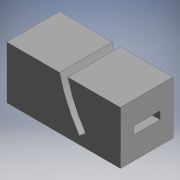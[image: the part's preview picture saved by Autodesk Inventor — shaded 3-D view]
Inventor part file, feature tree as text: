
AUTODESK INVENTOR PART (.ipt)
format: ipt  version: 2018 (Build 220112000, 112)  size: 113,664 bytes
history: native  units: in
note: dims shown in document units (in); Inventor stores cm internally (conversion verified against a paired STEP export)
features: extrude x2, sketch x2
ambient origin geometry x8: Origin, YZ Plane, XZ Plane, XY Plane, X Axis, Y Axis, Z Axis, Center Point
bodies: Solid1 (feature_tree)
feature tree (4):
  extrude  "Extrusion1"  Depth=0.3937in
  extrude  "Extrusion2"  Depth=0.3937in TaperAngle=0.0deg
  sketch  "Sketch1"  dims[d0=0.3937in d2=0.3937in]
  sketch  "Sketch2"  dims[d4=0.3937in d5=0.3937in d6=0.0in d7=0.1969in d8=0.0591in d9=0.3937in d10=0.0in d11=0.0591in d12=0.0591in d13=1.378in d14=0.6299in]
